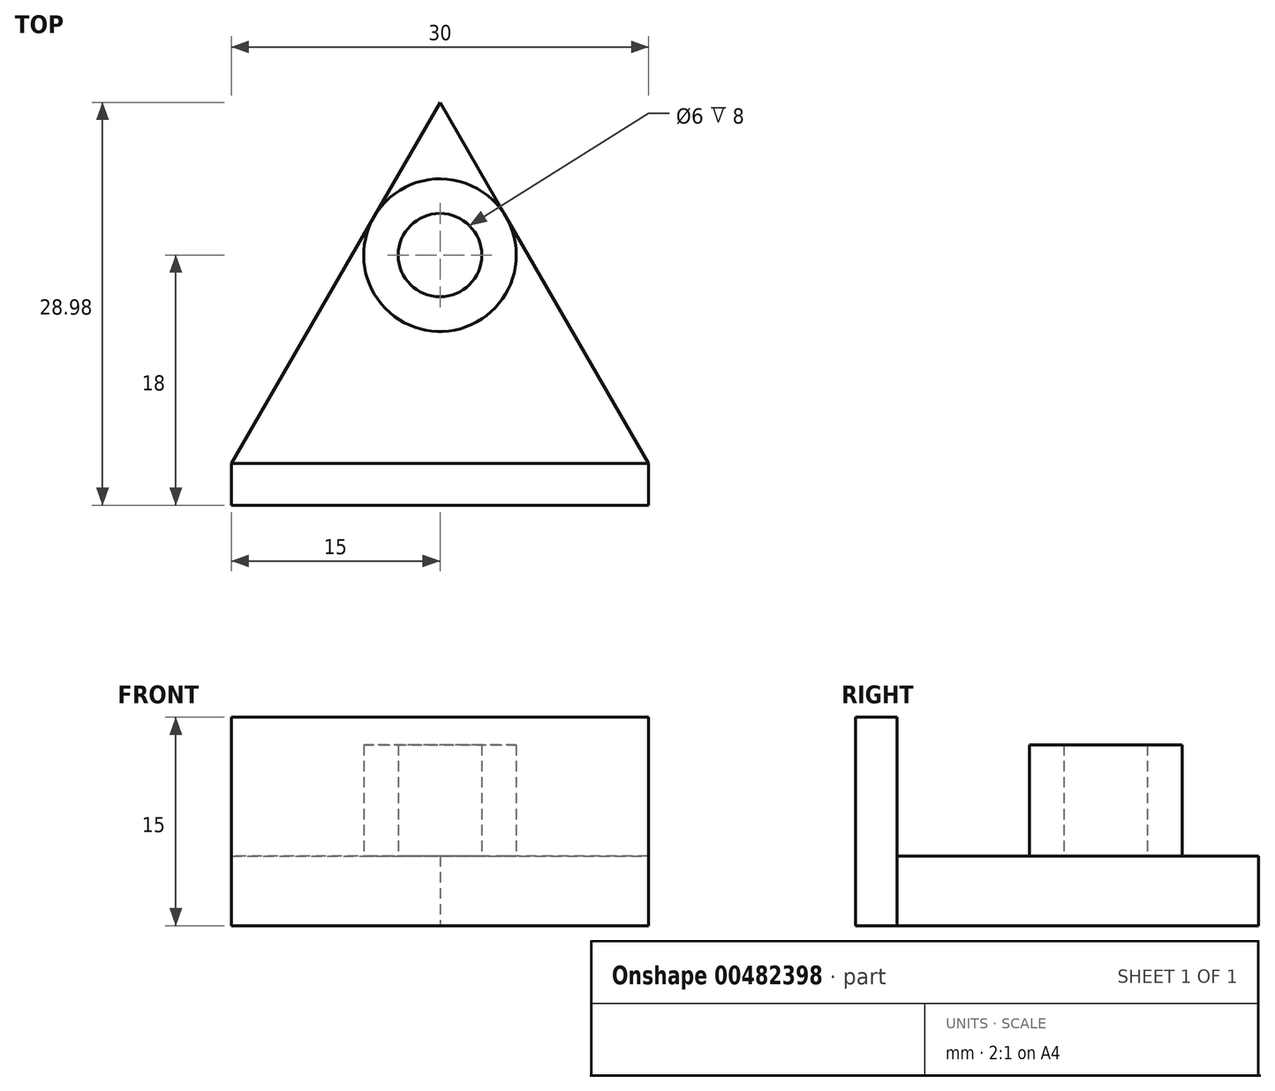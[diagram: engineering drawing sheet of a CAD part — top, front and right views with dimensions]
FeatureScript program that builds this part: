
annotation { "Feature Type Name" : "Feature", "Feature Type Description" : "" }
export const myFeature = defineFeature(function(context is Context, id is Id, definition is map)
    precondition{}
    {
        {
            var Q0;
            Q0=qCreatedBy(makeId("Top.planeOp"),FACE);
            var sketch = newSketch(context, id + "F0", { "sketchPlane" : qUnion([Q0])});
            skLineSegment(sketch, "E0", {"start": v(-15, 0) * mm, "end": v(15, 0) * mm});
            skLineSegment(sketch, "E1", {"start": v(15, 0) * mm, "end": v(0, 25.98) * mm});
            skLineSegment(sketch, "E2", {"start": v(0, 25.98) * mm, "end": v(-15, 0) * mm});
            skSolve(sketch);
        }
        {
            var Q0;
            Q0 = qSketchRegion(id + "F0", true);
            extrude(context, id + "F1", {"entities" : qUnion([Q0]), "depth" : 5 * mm});
        }
        {
            var Q0;
            Q0=makeQuery(id+"F1.opExtrude","SWEPT_FACE",FACE,{"disambiguationData":[OSD([sQuery(id+"F0.wireOp",EDGE,"E0")])]});
            var sketch = newSketch(context, id + "F2", { "sketchPlane" : qUnion([Q0])});
            skPoint(sketch, "E3.oppositeSnap0", {"position": v(15, 2.5) * mm});
            skLineSegment(sketch, "E3.bottom", {"start": v(-15, 0) * mm, "end": v(15, 0) * mm});
            skLineSegment(sketch, "E3.top", {"start": v(-15, 15) * mm, "end": v(15, 15) * mm});
            skLineSegment(sketch, "E3.left", {"start": v(-15, 0) * mm, "end": v(-15, 15) * mm});
            skLineSegment(sketch, "E3.right", {"start": v(15, 0) * mm, "end": v(15, 15) * mm});
            skSolve(sketch);
        }
        {
            var Q0;
            Q0 = qSketchRegion(id + "F2", true);
            extrude(context, id + "F3", {"entities" : qUnion([Q0]), "operationType" : NewBodyOperationType.ADD, "depth" : 3 * mm});
        }
        {
            var Q0;
            Q0=makeQuery(id+"F1.opExtrude","CAP_FACE",FACE,{"disambiguationData":[OSD([sQuery(id+"F0.wireOp",EDGE,"E0"),sQuery(id+"F0.wireOp",EDGE,"E1"),sQuery(id+"F0.wireOp",EDGE,"E2")])],"isStart":false});
            var sketch = newSketch(context, id + "F4", { "sketchPlane" : qUnion([Q0])});
            skCircle(sketch, "E4", {"center": v(0, 15) * mm, "radius": 5.5 * mm});
            skCircle(sketch, "E5", {"center": v(0, 15) * mm, "radius": 3 * mm});
            skSolve(sketch);
        }
        {
            var Q0;
            Q0 = qSketchRegion(id + "F4", true);
            extrude(context, id + "F5", {"entities" : qUnion([Q0]), "operationType" : NewBodyOperationType.ADD, "depth" : 8 * mm});
        }
    });
